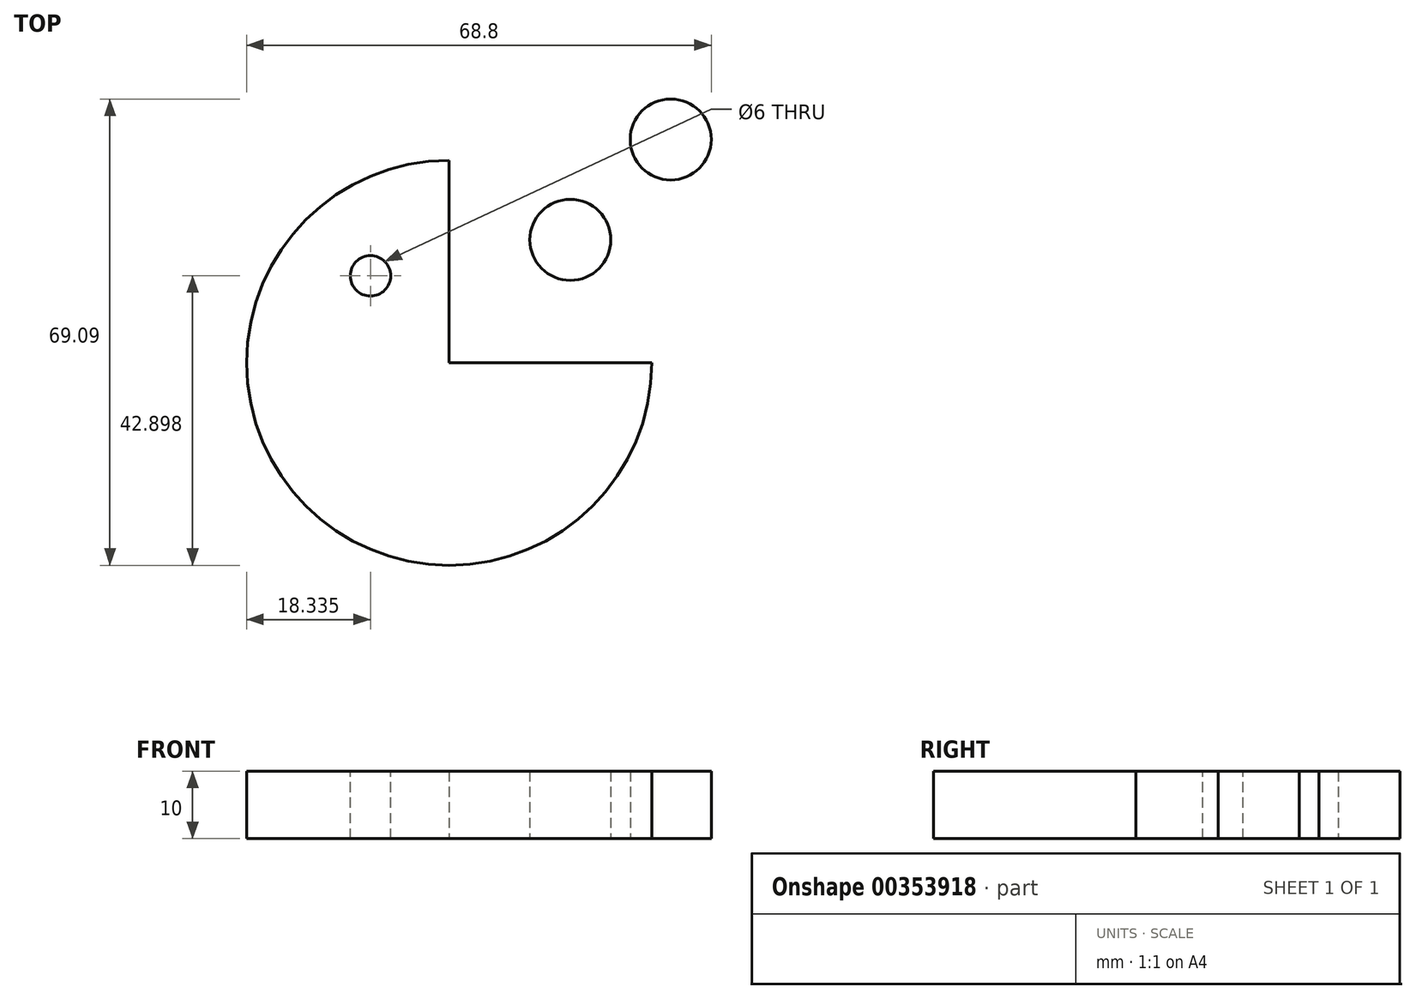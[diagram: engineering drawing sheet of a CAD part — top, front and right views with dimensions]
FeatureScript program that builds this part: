
annotation { "Feature Type Name" : "Feature", "Feature Type Description" : "" }
export const myFeature = defineFeature(function(context is Context, id is Id, definition is map)
    precondition{}
    {
        {
            var Q0;
            Q0=qCreatedBy(makeId("Top.planeOp"),FACE);
            var sketch = newSketch(context, id + "F0", { "sketchPlane" : qUnion([Q0])});
            skArc(sketch, "E0", {"start": v(0, 30) * mm, "mid": v(-21.21, -21.21) * mm, "end": v(30, 0) * mm});
            skLineSegment(sketch, "E1", {"start": v(0, 0) * mm, "end": v(0, 30) * mm});
            skLineSegment(sketch, "E2", {"start": v(0, 0) * mm, "end": v(30, 0) * mm});
            skSolve(sketch);
        }
        {
            var Q0;
            Q0=makeQuery(id+"F0.imprint","IMPRINT",FACE,{"disambiguationData":[TD([[makeQuery(id+"F0.imprint","IMPRINT",EDGE,{"derivedFrom":sQuery(id+"F0.wireOp",EDGE,"E0")}),1.0]])]});
            extrude(context, id + "F1", {"entities" : qUnion([Q0]), "depth" : 10 * mm});
        }
        {
            var Q0;
            Q0=makeQuery(id+"F1.opExtrude","CAP_FACE",FACE,{"disambiguationData":[OSD([sQuery(id+"F0.wireOp",EDGE,"E0"),sQuery(id+"F0.wireOp",EDGE,"E1"),sQuery(id+"F0.wireOp",EDGE,"E2")])],"isStart":false});
            var sketch = newSketch(context, id + "F2", { "sketchPlane" : qUnion([Q0])});
            skCircle(sketch, "E3", {"center": v(-11.66, 12.9) * mm, "radius": 3 * mm});
            skSolve(sketch);
        }
        {
            var Q0;
            Q0=makeQuery(id+"F2.imprint","IMPRINT",FACE,{"disambiguationData":[TD([[makeQuery(id+"F2.imprint","IMPRINT",EDGE,{"derivedFrom":sQuery(id+"F2.wireOp",EDGE,"E3")}),1.0]])]});
            extrude(context, id + "F3", {"entities" : qUnion([Q0]), "operationType" : NewBodyOperationType.REMOVE, "oppositeDirection" : true, "depth" : 10 * mm});
        }
        {
            var Q0;
            Q0=qCreatedBy(makeId("Top.planeOp"),FACE);
            var sketch = newSketch(context, id + "F4", { "sketchPlane" : qUnion([Q0])});
            skCircle(sketch, "E4", {"center": v(17.93, 18.21) * mm, "radius": 6 * mm});
            skCircle(sketch, "E5", {"center": v(33.6, 33.09) * mm, "radius": 6 * mm});
            skSolve(sketch);
        }
        {
            var Q0;
            Q0=makeQuery(id+"F4.imprint","IMPRINT",FACE,{"disambiguationData":[TD([[makeQuery(id+"F4.imprint","IMPRINT",EDGE,{"derivedFrom":sQuery(id+"F4.wireOp",EDGE,"E4")}),1.0]])]});
            extrude(context, id + "F5", {"entities" : qUnion([Q0]), "depth" : 10 * mm});
        }
        {
            var Q0;
            Q0=qCreatedBy(makeId("Top.planeOp"),FACE);
            var sketch = newSketch(context, id + "F6", { "sketchPlane" : qUnion([Q0])});
            skCircle(sketch, "E6", {"center": v(32.8, 33.09) * mm, "radius": 6 * mm});
            skSolve(sketch);
        }
        {
            var Q0;
            Q0=makeQuery(id+"F6.imprint","IMPRINT",FACE,{"disambiguationData":[TD([[makeQuery(id+"F6.imprint","IMPRINT",EDGE,{"derivedFrom":sQuery(id+"F6.wireOp",EDGE,"E6")}),1.0]])]});
            extrude(context, id + "F7", {"entities" : qUnion([Q0]), "depth" : 10 * mm});
        }
    });
